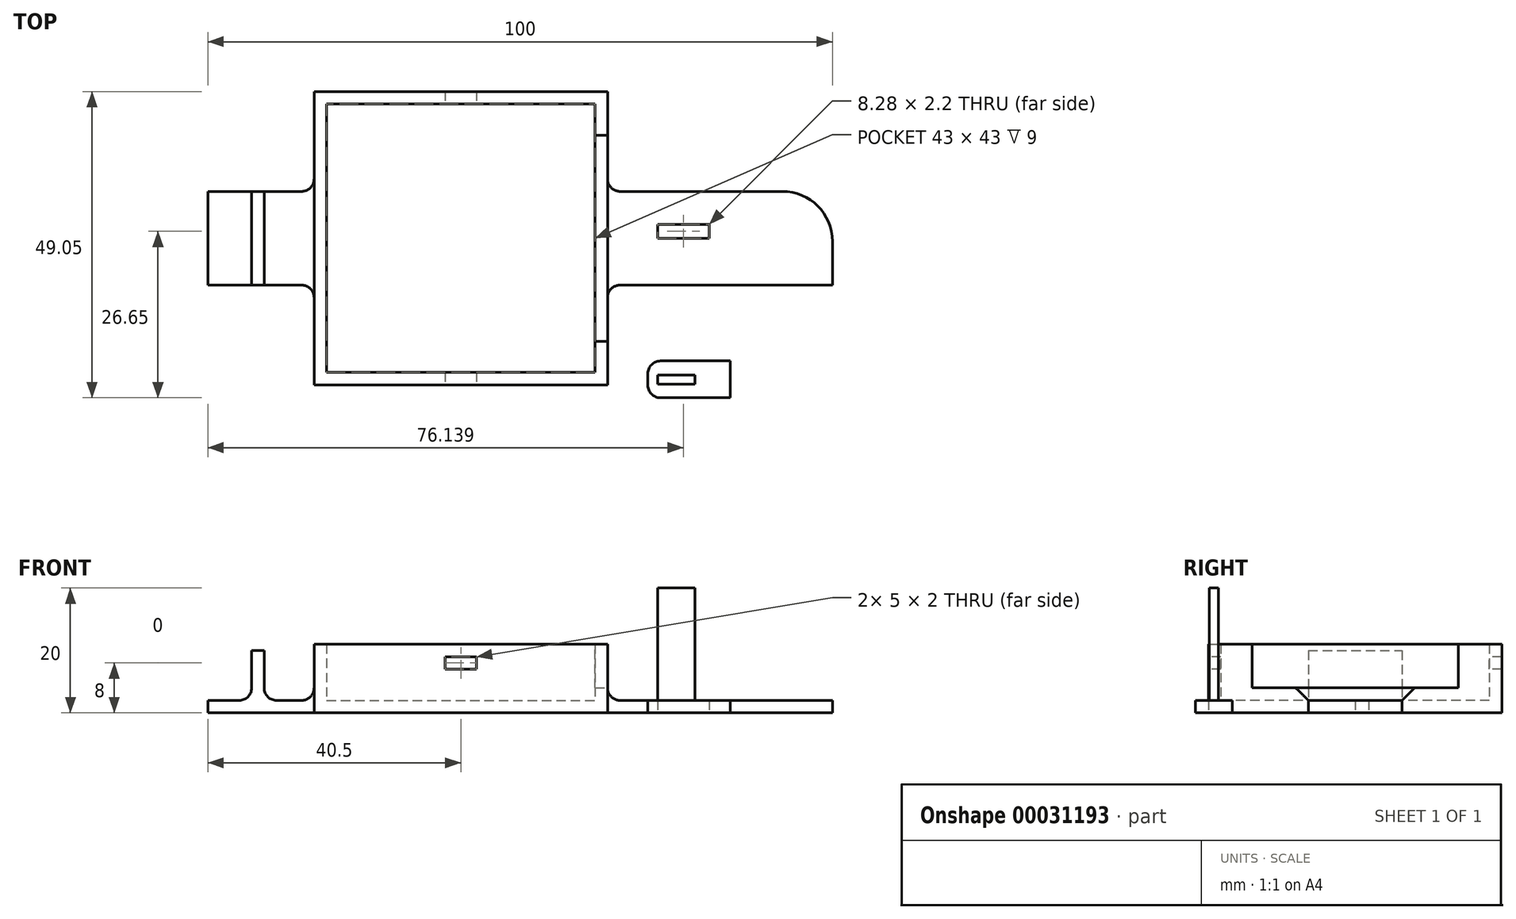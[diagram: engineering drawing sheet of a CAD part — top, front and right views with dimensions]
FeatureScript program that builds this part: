
annotation { "Feature Type Name" : "Feature", "Feature Type Description" : "" }
export const myFeature = defineFeature(function(context is Context, id is Id, definition is map)
    precondition{}
    {
        {
            var Q0;
            Q0=qCreatedBy(makeId("Top.planeOp"),FACE);
            var sketch = newSketch(context, id + "F0", { "sketchPlane" : qUnion([Q0])});
            skLineSegment(sketch, "E0.bottom", {"start": v(40.5, -7.5) * mm, "end": v(23.5, -7.5) * mm});
            skLineSegment(sketch, "E0.top", {"start": v(40.5, 7.5) * mm, "end": v(23.5, 7.5) * mm});
            skLineSegment(sketch, "E0.right", {"start": v(-40.5, -7.5) * mm, "end": v(-40.5, 7.5) * mm});
            skPoint(sketch, "E0.middle", {"position": v(0, 0) * mm});
            skLineSegment(sketch, "E1.bottom", {"start": v(21.5, -21.5) * mm, "end": v(-21.5, -21.5) * mm});
            skLineSegment(sketch, "E1.top", {"start": v(21.5, 21.5) * mm, "end": v(-21.5, 21.5) * mm});
            skLineSegment(sketch, "E1.left", {"start": v(21.5, -21.5) * mm, "end": v(21.5, 21.5) * mm});
            skLineSegment(sketch, "E1.right", {"start": v(-21.5, -21.5) * mm, "end": v(-21.5, 21.5) * mm});
            skLineSegment(sketch, "E2", {"start": v(-33.5, -7.5) * mm, "end": v(-40.5, -7.5) * mm});
            skLineSegment(sketch, "E3", {"start": v(-40.5, 7.5) * mm, "end": v(-33.5, 7.5) * mm});
            skLineSegment(sketch, "E4.trimOffspring", {"start": v(-23.5, 7.5) * mm, "end": v(-40.5, 7.5) * mm});
            skLineSegment(sketch, "E5.trimOffspring", {"start": v(-23.5, -7.5) * mm, "end": v(-40.5, -7.5) * mm});
            skLineSegment(sketch, "E6", {"start": v(40.5, 7.5) * mm, "end": v(51.5, 7.5) * mm});
            skLineSegment(sketch, "E7", {"start": v(59.5, -0.5) * mm, "end": v(59.5, -7.5) * mm});
            skLineSegment(sketch, "E8", {"start": v(59.5, -7.5) * mm, "end": v(40.5, -7.5) * mm});
            skLineSegment(sketch, "E9.0", {"start": v(23.5, 23.5) * mm, "end": v(-23.5, 23.5) * mm});
            skLineSegment(sketch, "E9.1", {"start": v(23.5, -23.5) * mm, "end": v(23.5, -7.5) * mm});
            skLineSegment(sketch, "E9.2", {"start": v(23.5, -23.5) * mm, "end": v(-23.5, -23.5) * mm});
            skLineSegment(sketch, "E9.3", {"start": v(-23.5, -23.5) * mm, "end": v(-23.5, -7.5) * mm});
            skPoint(sketch, "E10.orphan", {"position": v(21.5, -7.5) * mm});
            skPoint(sketch, "E11.orphan", {"position": v(-21.5, 7.5) * mm});
            skPoint(sketch, "E12.visualSharp", {"position": v(59.5, 7.5) * mm});
            skArc(sketch, "E12.filletArc", {"start": v(59.5, -0.5) * mm, "mid": v(57.16, 5.16) * mm, "end": v(51.5, 7.5) * mm});
            skPoint(sketch, "E13.end.orphan", {"position": v(-31.5, -7.5) * mm});
            skLineSegment(sketch, "E14.trimOffspring", {"start": v(-23.5, 7.5) * mm, "end": v(-23.5, 23.5) * mm});
            skLineSegment(sketch, "E15.trimOffspring", {"start": v(23.5, 7.5) * mm, "end": v(23.5, 23.5) * mm});
            skLineSegment(sketch, "E16", {"start": v(-33.5, -7.5) * mm, "end": v(-33.5, 7.5) * mm});
            skLineSegment(sketch, "E17", {"start": v(-31.5, -7.5) * mm, "end": v(-31.5, 7.5) * mm});
            skLineSegment(sketch, "E18.1", {"start": v(23.5, -23.5) * mm, "end": v(23.5, 23.5) * mm});
            skLineSegment(sketch, "E18.3", {"start": v(-23.5, -23.5) * mm, "end": v(-23.5, 23.5) * mm});
            skLineSegment(sketch, "E19", {"start": v(-31.5, 5.5) * mm, "end": v(-23.5, 5.5) * mm});
            skLineSegment(sketch, "E20", {"start": v(23.5, -5.5) * mm, "end": v(59.5, -5.5) * mm});
            skLineSegment(sketch, "E21", {"start": v(36.5, 7.5) * mm, "end": v(36.5, 2.2) * mm});
            skLineSegment(sketch, "E22.bottom", {"start": v(31.5, 0) * mm, "end": v(36.5, 0) * mm});
            skLineSegment(sketch, "E22.top", {"start": v(31.5, 2.2) * mm, "end": v(36.5, 2.2) * mm});
            skLineSegment(sketch, "E22.left", {"start": v(31.5, 0) * mm, "end": v(31.5, 2.2) * mm});
            skLineSegment(sketch, "E23", {"start": v(36.5, 2.2) * mm, "end": v(39.78, 2.2) * mm});
            skPoint(sketch, "E23.endSnap0", {"position": v(34, 2.2) * mm});
            skLineSegment(sketch, "E24", {"start": v(39.78, 2.2) * mm, "end": v(39.78, 0) * mm});
            skLineSegment(sketch, "E25", {"start": v(39.78, 0) * mm, "end": v(36.5, 0) * mm});
            skLineSegment(sketch, "E26.trimOffspring", {"start": v(36.5, 0) * mm, "end": v(36.5, -5.5) * mm});
            skSolve(sketch);
        }
        {
            var Q0;
            Q0 = qSketchRegion(id + "F0", true);
            var Q1;
            Q1=makeQuery(id+"F0.imprint","IMPRINT",FACE,{"disambiguationData":[TD([[makeQuery(id+"F0.imprint","IMPRINT",EDGE,{"derivedFrom":sQuery(id+"F0.wireOp",EDGE,"E1.bottom")}),-1.0]])]});
            extrude(context, id + "F1", {"entities" : qUnion([Q0, Q1]), "depth" : 2 * mm});
        }
        {
            var Q0;
            {var subQ0=sQuery(id+"F0.wireOp",EDGE,"E16");Q0=makeQuery(id+"F0.imprint","IMPRINT",FACE,{"disambiguationData":[TD([[makeQuery(id+"F0.imprint","IMPRINT",EDGE,{"derivedFrom":subQ0}),-1.0]])]});}
            extrude(context, id + "F2", {"entities" : qUnion([Q0]), "operationType" : NewBodyOperationType.ADD, "depth" : 10 * mm});
        }
        {
            var Q0;
            Q0=makeQuery(id+"F0.imprint","IMPRINT",FACE,{"disambiguationData":[TD([[makeQuery(id+"F0.imprint","IMPRINT",EDGE,{"derivedFrom":sQuery(id+"F0.wireOp",EDGE,"E1.bottom")}),1.0]])]});
            extrude(context, id + "F3", {"entities" : qUnion([Q0]), "operationType" : NewBodyOperationType.ADD, "depth" : 11 * mm});
        }
        {
            var Q0;
            {var subQ0=sQuery(id+"F0.wireOp",EDGE,"E18.1");Q0=makeQuery(id+"F3.boolean.opBoolean","MERGE",FACE,{"derivedFrom":[makeQuery(id+"F1.opExtrude","SWEPT_FACE",FACE,{"disambiguationData":[OSD([subQ0]),TDD([makeQuery(id+"F0.imprint","IMPRINT",EDGE,{"disambiguationData":[TD([[makeQuery(id+"F0.imprint","INTERSECT",VERTEX,{"derivedFrom":[sQuery(id+"F0.wireOp",EDGE,"E0.bottom"),subQ0]}),1.0]])],"derivedFrom":subQ0})])]}),makeQuery(id+"F1.opExtrude","SWEPT_FACE",FACE,{"disambiguationData":[OSD([subQ0]),TDD([makeQuery(id+"F0.imprint","IMPRINT",EDGE,{"disambiguationData":[TD([[makeQuery(id+"F0.imprint","INTERSECT",VERTEX,{"derivedFrom":[sQuery(id+"F0.wireOp",EDGE,"E0.top"),subQ0]}),-1.0]])],"derivedFrom":subQ0})])]}),makeQuery(id+"F3.opExtrude","SWEPT_FACE",FACE,{"disambiguationData":[OSD([subQ0])]})]});}
            var sketch = newSketch(context, id + "F4", { "sketchPlane" : qUnion([Q0])});
            skLineSegment(sketch, "E27", {"start": v(-16.5, 11) * mm, "end": v(-16.5, 4) * mm});
            skLineSegment(sketch, "E28", {"start": v(-16.5, 4) * mm, "end": v(16.5, 4) * mm});
            skLineSegment(sketch, "E29", {"start": v(16.5, 4) * mm, "end": v(16.5, 11) * mm});
            skLineSegment(sketch, "E30", {"start": v(16.5, 11) * mm, "end": v(-16.5, 11) * mm});
            skSolve(sketch);
        }
        {
            var Q0;
            Q0 = qSketchRegion(id + "F4", true);
            extrude(context, id + "F5", {"entities" : qUnion([Q0]), "operationType" : NewBodyOperationType.REMOVE, "oppositeDirection" : true, "depth" : 25 * mm});
        }
        {
            var Q0;
            {var subQ0=sQuery(id+"F0.wireOp",EDGE,"E18.3");var subQ1=sQuery(id+"F0.wireOp",EDGE,"E18.1");var subQ2=sQuery(id+"F0.wireOp",EDGE,"E0.top");var subQ3=sQuery(id+"F0.wireOp",EDGE,"E9.0");var subQ4=sQuery(id+"F0.wireOp",EDGE,"E12.filletArc");var subQ5=sQuery(id+"F0.wireOp",EDGE,"E7");var subQ6=sQuery(id+"F0.wireOp",EDGE,"E8");var subQ7=sQuery(id+"F0.wireOp",EDGE,"E0.bottom");var subQ8=sQuery(id+"F0.wireOp",EDGE,"E5.trimOffspring");var subQ9=sQuery(id+"F0.wireOp",EDGE,"E9.2");var subQ10=sQuery(id+"F0.wireOp",EDGE,"E6");var subQ11=sQuery(id+"F0.wireOp",EDGE,"E4.trimOffspring");Q0=makeQuery(id+"F3.boolean.opBoolean","INTERSECT",EDGE,{"derivedFrom":[makeQuery(id+"F2.boolean.opBoolean","SPLIT",FACE,{"disambiguationData":[TD([makeQuery(id+"F1.opExtrude","SWEPT_FACE",FACE,{"disambiguationData":[OSD([subQ5])]})])],"derivedFrom":makeQuery(id+"F1.opExtrude","CAP_FACE",FACE,{"disambiguationData":[OSD([subQ7,subQ2,sQuery(id+"F0.wireOp",EDGE,"E0.right"),subQ11,subQ8,subQ10,subQ5,subQ6,subQ4,subQ3,subQ1,subQ9,subQ0])],"isStart":false})}),makeQuery(id+"F3.opExtrude","SWEPT_FACE",FACE,{"disambiguationData":[OSD([subQ0])]})]});}
            var Q1;
            Q1=makeQuery(id+"F2.boolean.opBoolean","INTERSECT",EDGE,{"derivedFrom":[makeQuery(id+"F1.opExtrude","CAP_FACE",FACE,{"disambiguationData":[OSD([sQuery(id+"F0.wireOp",EDGE,"E0.bottom"),sQuery(id+"F0.wireOp",EDGE,"E0.top"),sQuery(id+"F0.wireOp",EDGE,"E0.right"),sQuery(id+"F0.wireOp",EDGE,"E4.trimOffspring"),sQuery(id+"F0.wireOp",EDGE,"E5.trimOffspring"),sQuery(id+"F0.wireOp",EDGE,"E6"),sQuery(id+"F0.wireOp",EDGE,"E7"),sQuery(id+"F0.wireOp",EDGE,"E8"),sQuery(id+"F0.wireOp",EDGE,"E12.filletArc"),sQuery(id+"F0.wireOp",EDGE,"E9.0"),sQuery(id+"F0.wireOp",EDGE,"E18.1"),sQuery(id+"F0.wireOp",EDGE,"E9.2"),sQuery(id+"F0.wireOp",EDGE,"E18.3")])],"isStart":false}),makeQuery(id+"F2.opExtrude","SWEPT_FACE",FACE,{"disambiguationData":[OSD([sQuery(id+"F0.wireOp",EDGE,"E17")])]})]});
            var Q2;
            {var subQ0=sQuery(id+"F0.wireOp",EDGE,"E18.1");var subQ1=sQuery(id+"F0.wireOp",EDGE,"E0.top");var subQ2=sQuery(id+"F0.wireOp",EDGE,"E9.0");var subQ3=sQuery(id+"F0.wireOp",EDGE,"E12.filletArc");var subQ4=sQuery(id+"F0.wireOp",EDGE,"E7");var subQ5=sQuery(id+"F0.wireOp",EDGE,"E8");var subQ6=sQuery(id+"F0.wireOp",EDGE,"E0.bottom");var subQ7=sQuery(id+"F0.wireOp",EDGE,"E18.3");var subQ8=sQuery(id+"F0.wireOp",EDGE,"E5.trimOffspring");var subQ9=sQuery(id+"F0.wireOp",EDGE,"E9.2");var subQ10=sQuery(id+"F0.wireOp",EDGE,"E6");var subQ11=sQuery(id+"F0.wireOp",EDGE,"E4.trimOffspring");Q2=makeQuery(id+"F3.boolean.opBoolean","INTERSECT",EDGE,{"derivedFrom":[makeQuery(id+"F2.boolean.opBoolean","SPLIT",FACE,{"disambiguationData":[TD([makeQuery(id+"F1.opExtrude","SWEPT_FACE",FACE,{"disambiguationData":[OSD([subQ4])]})])],"derivedFrom":makeQuery(id+"F1.opExtrude","CAP_FACE",FACE,{"disambiguationData":[OSD([subQ6,subQ1,sQuery(id+"F0.wireOp",EDGE,"E0.right"),subQ11,subQ8,subQ10,subQ4,subQ5,subQ3,subQ2,subQ0,subQ9,subQ7])],"isStart":false})}),makeQuery(id+"F3.opExtrude","SWEPT_FACE",FACE,{"disambiguationData":[OSD([subQ0])]})]});}
            var Q3;
            Q3=makeQuery(id+"F2.boolean.opBoolean","INTERSECT",EDGE,{"derivedFrom":[makeQuery(id+"F1.opExtrude","CAP_FACE",FACE,{"disambiguationData":[OSD([sQuery(id+"F0.wireOp",EDGE,"E0.bottom"),sQuery(id+"F0.wireOp",EDGE,"E0.top"),sQuery(id+"F0.wireOp",EDGE,"E0.right"),sQuery(id+"F0.wireOp",EDGE,"E4.trimOffspring"),sQuery(id+"F0.wireOp",EDGE,"E5.trimOffspring"),sQuery(id+"F0.wireOp",EDGE,"E6"),sQuery(id+"F0.wireOp",EDGE,"E7"),sQuery(id+"F0.wireOp",EDGE,"E8"),sQuery(id+"F0.wireOp",EDGE,"E12.filletArc"),sQuery(id+"F0.wireOp",EDGE,"E9.0"),sQuery(id+"F0.wireOp",EDGE,"E18.1"),sQuery(id+"F0.wireOp",EDGE,"E9.2"),sQuery(id+"F0.wireOp",EDGE,"E18.3")])],"isStart":false}),makeQuery(id+"F2.opExtrude","SWEPT_FACE",FACE,{"disambiguationData":[OSD([sQuery(id+"F0.wireOp",EDGE,"E16")])]})]});
            var Q4;
            {var subQ0=sQuery(id+"F0.wireOp",EDGE,"E18.1");var subQ1=sQuery(id+"F0.wireOp",EDGE,"E0.bottom");Q4=makeQuery(id+"FSCxSZ95IdE6EaA_0.boolean.opBoolean","MERGE",EDGE,{"derivedFrom":[makeQuery(id+"F1.opExtrude","SWEPT_EDGE",EDGE,{"disambiguationData":[OSD([subQ1,subQ0])]}),makeQuery(id+"FSCxSZ95IdE6EaA_0.opExtrude","SWEPT_EDGE",EDGE,{"disambiguationData":[OSD([subQ1,subQ0])]})]});}
            var Q5;
            Q5=makeQuery(id+"F1.opExtrude","SWEPT_EDGE",EDGE,{"disambiguationData":[OSD([sQuery(id+"F0.wireOp",EDGE,"E0.top"),sQuery(id+"F0.wireOp",EDGE,"E18.1")])]});
            var Q6;
            Q6=makeQuery(id+"F1.opExtrude","SWEPT_EDGE",EDGE,{"disambiguationData":[OSD([sQuery(id+"F0.wireOp",EDGE,"E5.trimOffspring"),sQuery(id+"F0.wireOp",EDGE,"E18.3")])]});
            var Q7;
            {var subQ0=sQuery(id+"F0.wireOp",EDGE,"E18.3");var subQ1=sQuery(id+"F0.wireOp",EDGE,"E4.trimOffspring");Q7=makeQuery(id+"FSCxSZ95IdE6EaA_0.boolean.opBoolean","MERGE",EDGE,{"derivedFrom":[makeQuery(id+"F1.opExtrude","SWEPT_EDGE",EDGE,{"disambiguationData":[OSD([subQ1,subQ0])]}),makeQuery(id+"FSCxSZ95IdE6EaA_0.opExtrude","SWEPT_EDGE",EDGE,{"disambiguationData":[OSD([subQ1,subQ0])]})]});}
            fillet(context, id + "F6", {"entities" : qUnion([Q0, Q1, Q2, Q3, Q4, Q5, Q6, Q7]), "radius" : 2 * mm, "tangentPropagation" : true, "allowEdgeOverflow" : false});
        }
        {
            var Q0;
            {var subQ0=sQuery(id+"F0.wireOp",EDGE,"E22.bottom");Q0=makeQuery(id+"F0.imprint","IMPRINT",FACE,{"disambiguationData":[TD([[makeQuery(id+"F0.imprint","IMPRINT",EDGE,{"derivedFrom":subQ0}),1.0]])]});}
            extrude(context, id + "F7", {"entities" : qUnion([Q0]), "operationType" : NewBodyOperationType.REMOVE, "oppositeDirection" : true, "depth" : 25 * mm});
        }
        {
            var Q0;
            {var subQ0=sQuery(id+"F0.wireOp",EDGE,"E9.2");Q0=makeQuery(id+"F3.boolean.opBoolean","MERGE",FACE,{"derivedFrom":[makeQuery(id+"F1.opExtrude","SWEPT_FACE",FACE,{"disambiguationData":[OSD([subQ0])]}),makeQuery(id+"F3.opExtrude","SWEPT_FACE",FACE,{"disambiguationData":[OSD([subQ0])]})]});}
            var sketch = newSketch(context, id + "F8", { "sketchPlane" : qUnion([Q0])});
            skLineSegment(sketch, "E31.bottom", {"start": v(2.5, 7) * mm, "end": v(-2.5, 7) * mm});
            skLineSegment(sketch, "E31.top", {"start": v(2.5, 9) * mm, "end": v(-2.5, 9) * mm});
            skLineSegment(sketch, "E31.left", {"start": v(2.5, 7) * mm, "end": v(2.5, 9) * mm});
            skLineSegment(sketch, "E31.right", {"start": v(-2.5, 7) * mm, "end": v(-2.5, 9) * mm});
            skPoint(sketch, "E31.middle", {"position": v(0, 8) * mm});
            skPoint(sketch, "E31.middle.positionSnap0", {"position": v(0, 11) * mm});
            skPoint(sketch, "E31.centerSnap0", {"position": v(0, 11) * mm});
            skSolve(sketch);
        }
        {
            var Q0;
            Q0=makeQuery(id+"F8.imprint","IMPRINT",FACE,{"disambiguationData":[TD([[makeQuery(id+"F8.imprint","IMPRINT",EDGE,{"derivedFrom":sQuery(id+"F8.wireOp",EDGE,"E31.bottom")}),-1.0]])]});
            extrude(context, id + "F9", {"entities" : qUnion([Q0]), "operationType" : NewBodyOperationType.REMOVE, "endBound" : BoundingType.THROUGH_ALL, "oppositeDirection" : true, "depth" : 25 * mm});
        }
        {
            var Q0;
            Q0=qCreatedBy(makeId("Top.planeOp"),FACE);
            var sketch = newSketch(context, id + "F10", { "sketchPlane" : qUnion([Q0])});
            skLineSegment(sketch, "E32", {"start": v(31.5, -21.9) * mm, "end": v(37.5, -21.9) * mm});
            skLineSegment(sketch, "E33", {"start": v(37.5, -21.9) * mm, "end": v(37.5, -23.4) * mm});
            skLineSegment(sketch, "E34", {"start": v(37.5, -23.4) * mm, "end": v(31.5, -23.4) * mm});
            skLineSegment(sketch, "E35", {"start": v(31.5, -23.4) * mm, "end": v(31.5, -21.9) * mm});
            skPoint(sketch, "E36.0.end.orphan", {"position": v(31.5, 2.2) * mm});
            skPoint(sketch, "E36.0.start.orphan", {"position": v(31.5, 0) * mm});
            skPoint(sketch, "E37.0.end.orphan", {"position": v(39.78, 0) * mm});
            skPoint(sketch, "E37.0.start.orphan", {"position": v(39.78, 2.2) * mm});
            skLineSegment(sketch, "E38.bottom", {"start": v(31.95, -19.67) * mm, "end": v(43.16, -19.67) * mm});
            skLineSegment(sketch, "E38.top", {"start": v(31.95, -25.55) * mm, "end": v(43.16, -25.55) * mm});
            skLineSegment(sketch, "E38.left", {"start": v(29.95, -21.67) * mm, "end": v(29.95, -23.55) * mm});
            skLineSegment(sketch, "E38.right", {"start": v(43.16, -19.67) * mm, "end": v(43.16, -25.55) * mm});
            skPoint(sketch, "E39.visualSharp", {"position": v(29.95, -19.67) * mm});
            skArc(sketch, "E39.filletArc", {"start": v(31.95, -19.67) * mm, "mid": v(30.54, -20.25) * mm, "end": v(29.95, -21.67) * mm});
            skPoint(sketch, "E40.visualSharp", {"position": v(29.95, -25.55) * mm});
            skArc(sketch, "E40.filletArc", {"start": v(29.95, -23.55) * mm, "mid": v(30.54, -24.97) * mm, "end": v(31.95, -25.55) * mm});
            skSolve(sketch);
        }
        {
            var Q0;
            Q0=makeQuery(id+"F10.imprint","IMPRINT",FACE,{"disambiguationData":[TD([[makeQuery(id+"F10.imprint","IMPRINT",EDGE,{"derivedFrom":sQuery(id+"F10.wireOp",EDGE,"E32")}),-1.0]])]});
            extrude(context, id + "F11", {"entities" : qUnion([Q0]), "depth" : 20 * mm});
        }
        {
            var Q0;
            Q0 = qSketchRegion(id + "F10", true);
            extrude(context, id + "F12", {"entities" : qUnion([Q0]), "operationType" : NewBodyOperationType.ADD, "depth" : 2 * mm});
        }
    });
